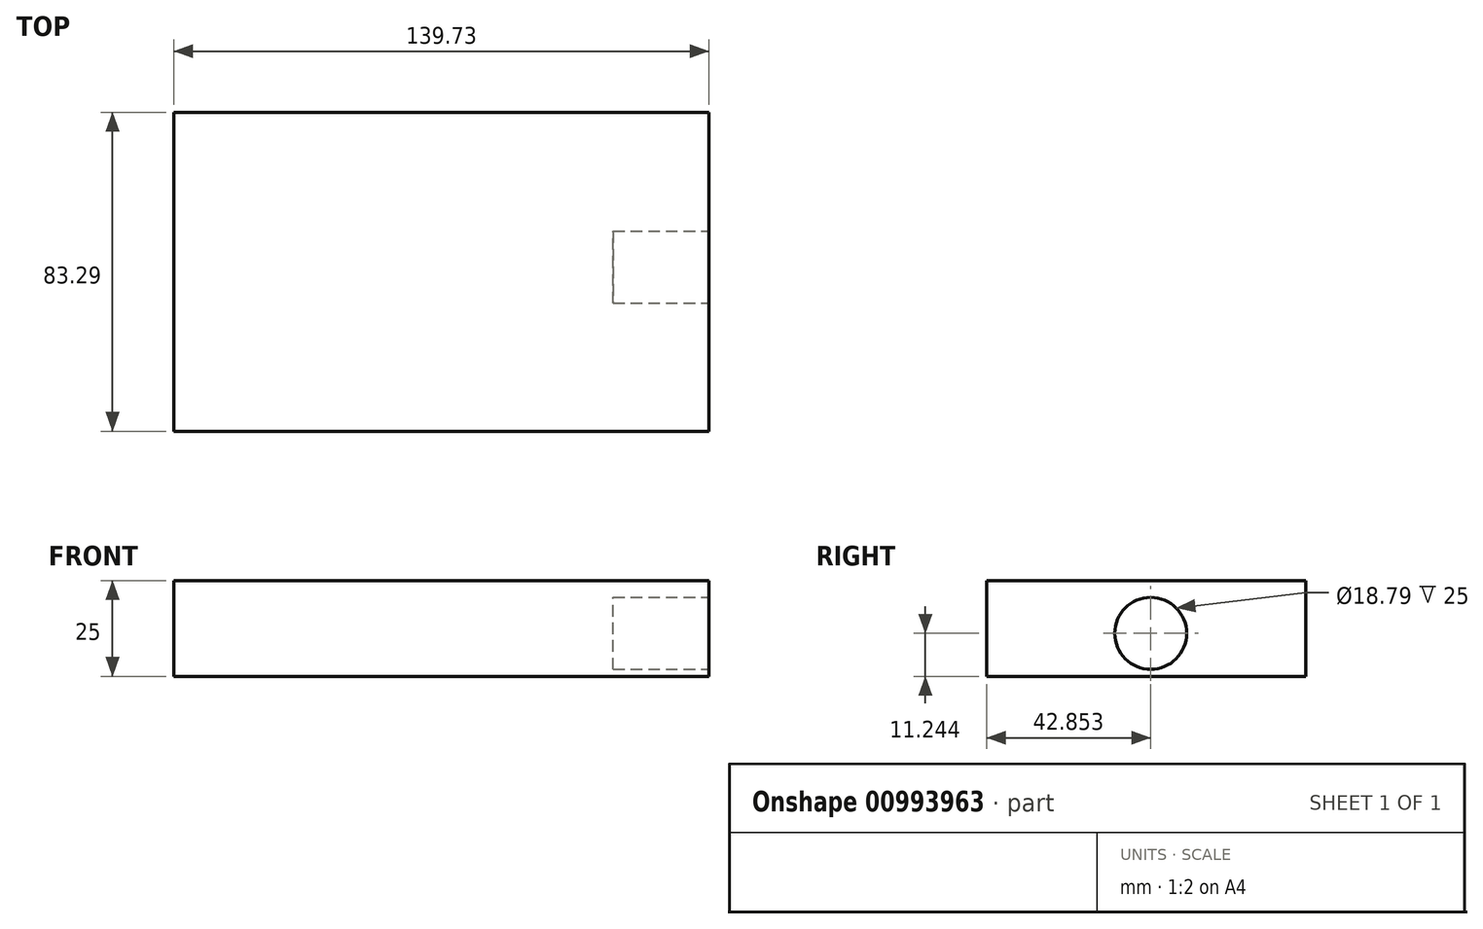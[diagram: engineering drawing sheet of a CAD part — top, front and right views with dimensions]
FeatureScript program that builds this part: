
annotation { "Feature Type Name" : "Feature", "Feature Type Description" : "" }
export const myFeature = defineFeature(function(context is Context, id is Id, definition is map)
    precondition{}
    {
        {
            var Q0;
            Q0=qCreatedBy(makeId("Top.planeOp"),FACE);
            var sketch = newSketch(context, id + "F0", { "sketchPlane" : qUnion([Q0])});
            skLineSegment(sketch, "E0.bottom", {"start": v(-92.3, 30.68) * mm, "end": v(47.42, 30.68) * mm});
            skLineSegment(sketch, "E0.top", {"start": v(-92.3, -52.6) * mm, "end": v(47.42, -52.6) * mm});
            skLineSegment(sketch, "E0.left", {"start": v(-92.3, 30.68) * mm, "end": v(-92.3, -52.6) * mm});
            skLineSegment(sketch, "E0.right", {"start": v(47.42, 30.68) * mm, "end": v(47.42, -52.6) * mm});
            skSolve(sketch);
        }
        {
            var Q0;
            Q0=makeQuery(id+"F0.imprint","IMPRINT",FACE,{"disambiguationData":[TD([[makeQuery(id+"F0.imprint","IMPRINT",EDGE,{"derivedFrom":sQuery(id+"F0.wireOp",EDGE,"E0.bottom")}),-1.0]])]});
            extrude(context, id + "F1", {"entities" : qUnion([Q0]), "depth" : 25 * mm, "offsetDistance" : 25 * mm});
        }
        {
            var Q0;
            Q0=makeQuery(id+"F1.opExtrude","SWEPT_FACE",FACE,{"disambiguationData":[OSD([sQuery(id+"F0.wireOp",EDGE,"E0.right")])]});
            var sketch = newSketch(context, id + "F2", { "sketchPlane" : qUnion([Q0])});
            skCircle(sketch, "E1", {"center": v(-9.76, 11.24) * mm, "radius": 9.4 * mm});
            skSolve(sketch);
        }
        {
            var Q0;
            Q0 = qSketchRegion(id + "F2", true);
            extrude(context, id + "F3", {"entities" : qUnion([Q0]), "operationType" : NewBodyOperationType.REMOVE, "oppositeDirection" : true, "depth" : 25 * mm, "offsetDistance" : 25 * mm});
        }
    });
